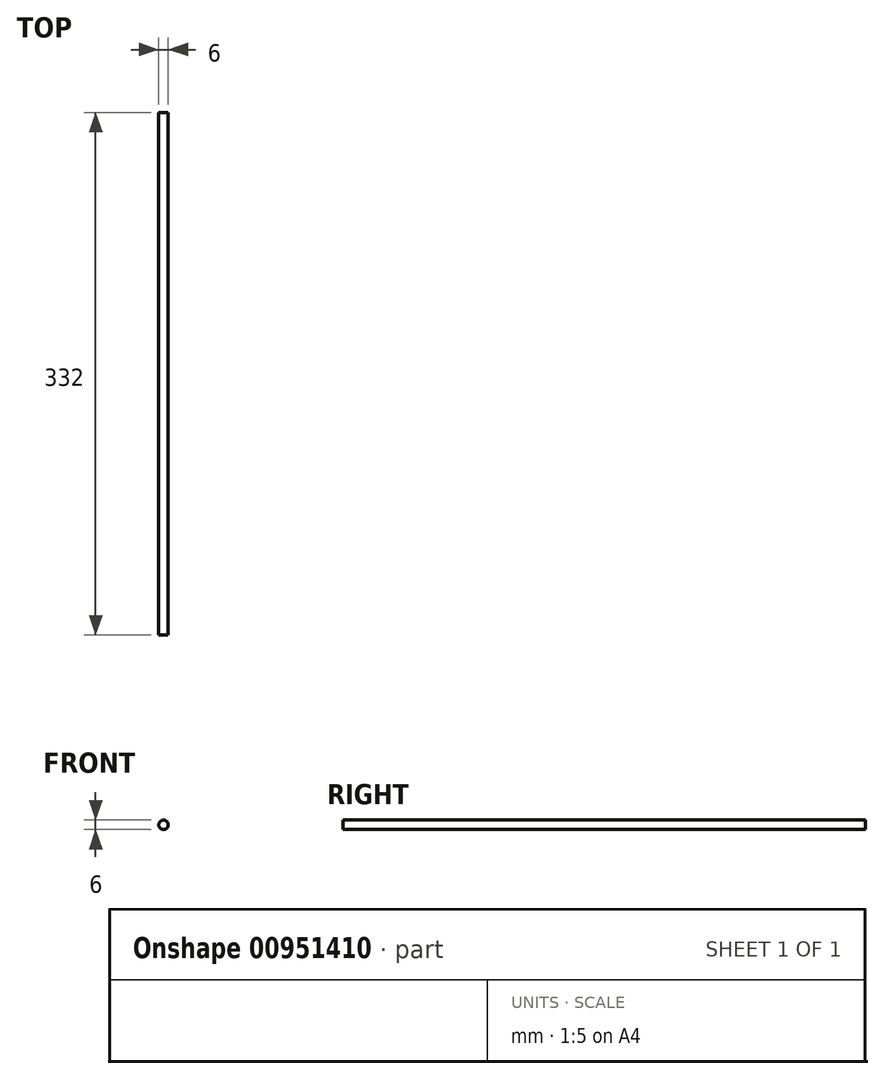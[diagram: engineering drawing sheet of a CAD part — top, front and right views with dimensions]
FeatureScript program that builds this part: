
annotation { "Feature Type Name" : "Feature", "Feature Type Description" : "" }
export const myFeature = defineFeature(function(context is Context, id is Id, definition is map)
    precondition{}
    {
        {
            var Q0;
            Q0=qCreatedBy(makeId("Front.planeOp"),FACE);
            var sketch = newSketch(context, id + "F0", { "sketchPlane" : qUnion([Q0])});
            skCircle(sketch, "E0", {"center": v(0, 0) * mm, "radius": 3 * mm});
            skSolve(sketch);
        }
        {
            var Q0;
            Q0 = qSketchRegion(id + "F0", true);
            extrude(context, id + "F1", {"entities" : qUnion([Q0]), "depth" : 332 * mm, "offsetDistance" : 25 * mm});
        }
    });
